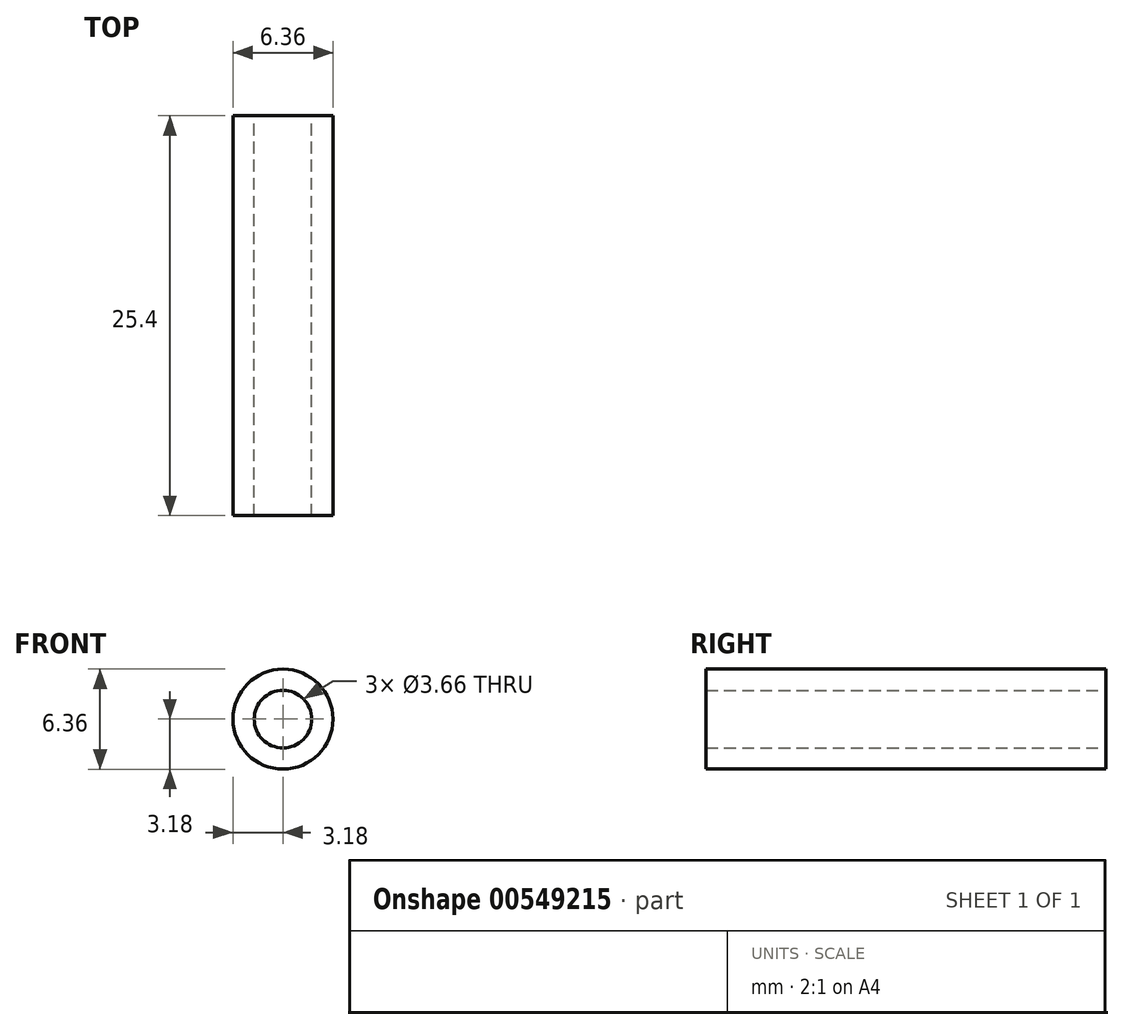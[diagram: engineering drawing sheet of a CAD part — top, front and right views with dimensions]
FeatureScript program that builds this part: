
annotation { "Feature Type Name" : "Feature", "Feature Type Description" : "" }
export const myFeature = defineFeature(function(context is Context, id is Id, definition is map)
    precondition{}
    {
        {
            var Q0;
            Q0=qCreatedBy(makeId("Front.planeOp"),FACE);
            var sketch = newSketch(context, id + "F0", { "sketchPlane" : qUnion([Q0])});
            skCircle(sketch, "E0", {"center": v(0, 0) * mm, "radius": 3.18 * mm});
            skCircle(sketch, "E1", {"center": v(0, 0) * mm, "radius": 1.83 * mm});
            skSolve(sketch);
        }
        {
            var Q0;
            Q0=makeQuery(id+"F0.imprint","IMPRINT",FACE,{"disambiguationData":[TD([[makeQuery(id+"F0.imprint","IMPRINT",EDGE,{"derivedFrom":sQuery(id+"F0.wireOp",EDGE,"E0")}),1.0]])]});
            extrude(context, id + "F1", {"entities" : qUnion([Q0]), "depth" : 25.4 * mm, "offsetDistance" : 25.4 * mm, "symmetric" : true});
        }
    });
